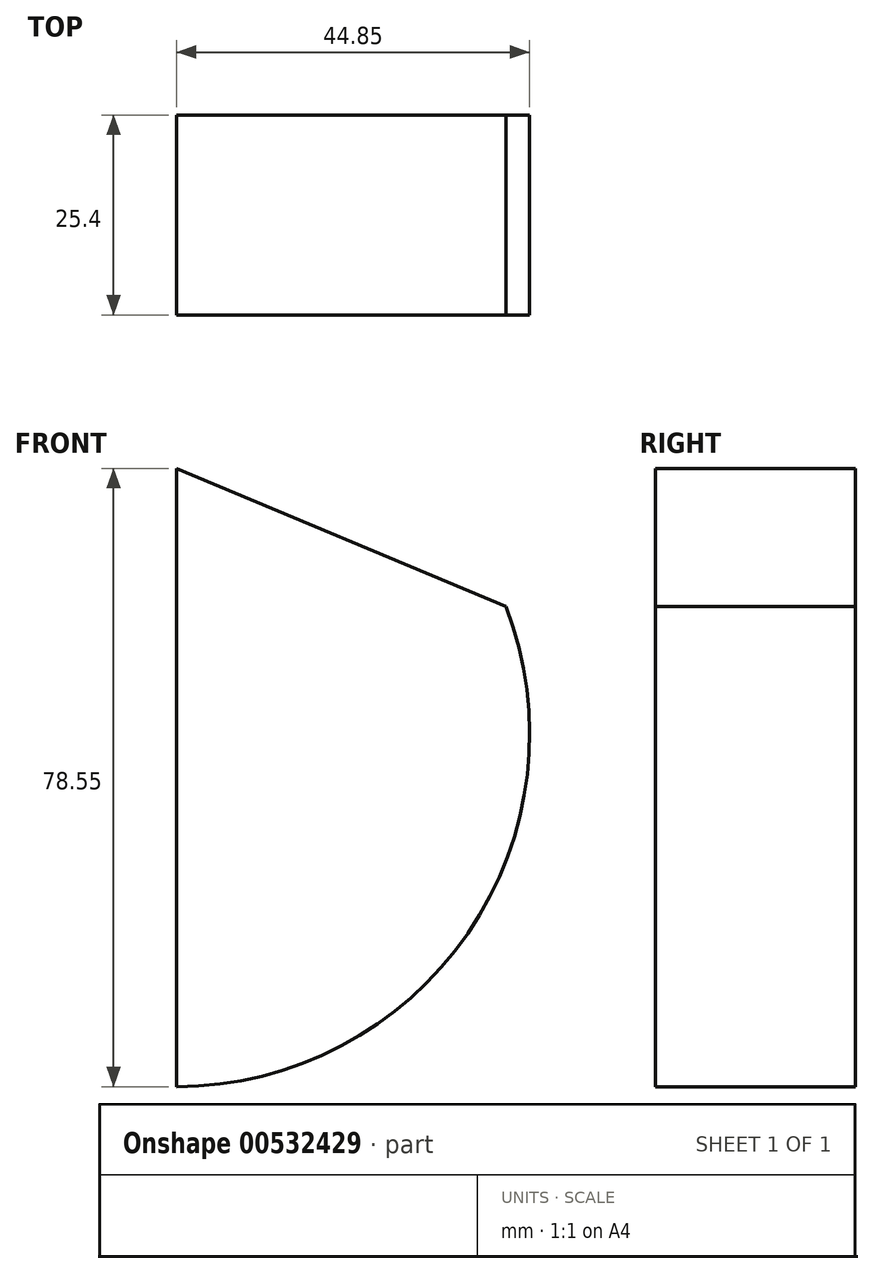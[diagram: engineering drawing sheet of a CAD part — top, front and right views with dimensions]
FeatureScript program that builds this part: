
annotation { "Feature Type Name" : "Feature", "Feature Type Description" : "" }
export const myFeature = defineFeature(function(context is Context, id is Id, definition is map)
    precondition{}
    {
        {
            var Q0;
            Q0=qCreatedBy(makeId("Front.planeOp"),FACE);
            var sketch = newSketch(context, id + "F0", { "sketchPlane" : qUnion([Q0])});
            skCircle(sketch, "E0", {"center": v(0, 0) * mm, "radius": 44.85 * mm});
            skLineSegment(sketch, "E1", {"start": v(0, 44.85) * mm, "end": v(0, -44.85) * mm});
            skLineSegment(sketch, "E2", {"start": v(0, 33.7) * mm, "end": v(41.83, 16.18) * mm});
            skSolve(sketch);
        }
        {
            var Q0;
            {var subQ0=sQuery(id+"F0.wireOp",EDGE,"E1");var subQ1=sQuery(id+"F0.wireOp",EDGE,"E0");var subQ2=makeQuery(id+"F0.imprint","INTERSECT",VERTEX,{"disambiguationData":[OD(0.0)],"derivedFrom":[subQ1,subQ0]});Q0=makeQuery(id+"F0.imprint","IMPRINT",FACE,{"disambiguationData":[TD([[makeQuery(id+"F0.imprint","IMPRINT",EDGE,{"disambiguationData":[TD([[subQ2,-1.0]])],"derivedFrom":subQ1}),1.0]])]});}
            var Q1;
            {var subQ3=sQuery(id+"F0.wireOp",EDGE,"E2");Q1=makeQuery(id+"F0.imprint","IMPRINT",FACE,{"disambiguationData":[TD([[makeQuery(id+"F0.imprint","IMPRINT",EDGE,{"derivedFrom":subQ3}),-1.0]])]});}
            var Q2;
            Q2=sQuery(id+"F0.wireOp",EDGE,"E0");
            extrude(context, id + "F1", {"entities" : qUnion([Q0, Q1]), "surfaceEntities" : qUnion([Q2]), "depth" : 25.4 * mm, "offsetDistance" : 25.4 * mm});
        }
        {
            var Q0;
            Q0=makeQuery(id+"F1.opExtrude","SWEPT_FACE",FACE,{"disambiguationData":[OSD([sQuery(id+"F0.wireOp",EDGE,"E2")])]});
            var sketch = newSketch(context, id + "F2", { "sketchPlane" : qUnion([Q0])});
            skLineSegment(sketch, "E3.bottom", {"start": v(-2.73, -19.75) * mm, "end": v(24.34, -19.75) * mm});
            skLineSegment(sketch, "E3.top", {"start": v(-2.73, -5.36) * mm, "end": v(24.34, -5.36) * mm});
            skLineSegment(sketch, "E3.left", {"start": v(-2.73, -19.75) * mm, "end": v(-2.73, -5.36) * mm});
            skLineSegment(sketch, "E3.right", {"start": v(24.34, -19.75) * mm, "end": v(24.34, -5.36) * mm});
            skSolve(sketch);
        }
        {
            var Q0;
            Q0=sQuery(id+"F2.wireOp",EDGE,"E3.left");
            var Q1;
            Q1=sQuery(id+"F2.wireOp",EDGE,"E3.bottom");
            extrude(context, id + "F3", {"bodyType" : ToolBodyType.SURFACE, "surfaceEntities" : qUnion([Q0, Q1]), "depth" : 25.4 * mm, "offsetDistance" : 25.4 * mm});
        }
    });
